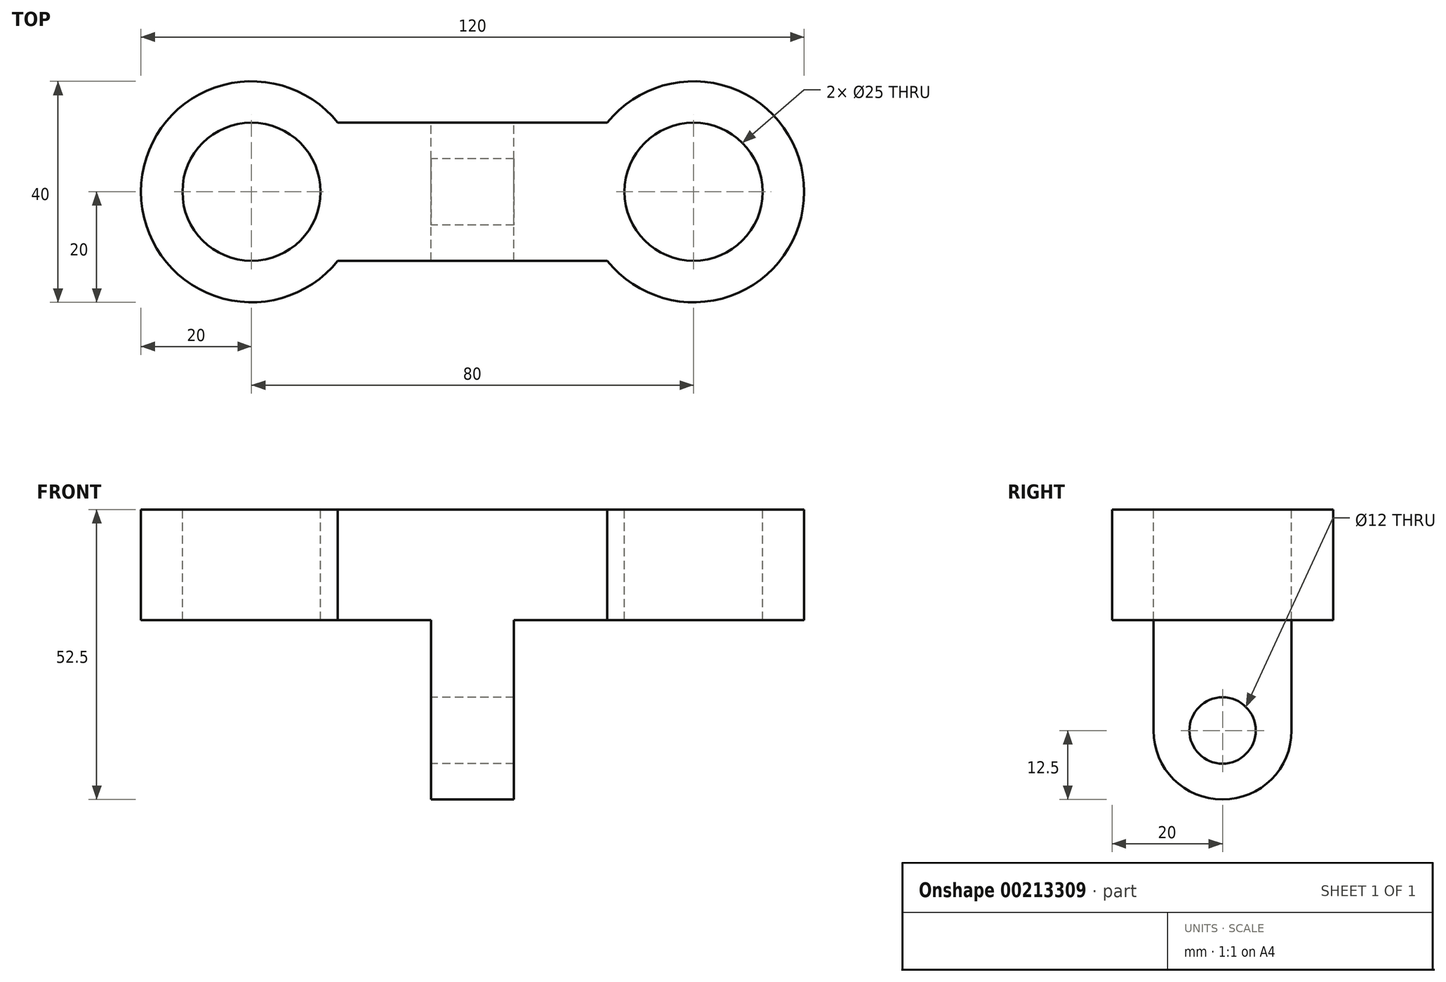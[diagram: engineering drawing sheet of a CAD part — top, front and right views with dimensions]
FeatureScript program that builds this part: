
annotation { "Feature Type Name" : "Feature", "Feature Type Description" : "" }
export const myFeature = defineFeature(function(context is Context, id is Id, definition is map)
    precondition{}
    {
        {
            var Q0;
            Q0=qCreatedBy(makeId("Top.planeOp"),FACE);
            var sketch = newSketch(context, id + "F0", { "sketchPlane" : qUnion([Q0])});
            skCircle(sketch, "E0", {"center": v(-40, 0) * mm, "radius": 12.5 * mm});
            skCircle(sketch, "E1", {"center": v(40, 0) * mm, "radius": 12.5 * mm});
            skArc(sketch, "E2", {"start": v(-24.39, 12.5) * mm, "mid": v(-60, 0) * mm, "end": v(-24.39, -12.5) * mm});
            skArc(sketch, "E3", {"start": v(24.39, -12.5) * mm, "mid": v(60, 0) * mm, "end": v(24.39, 12.5) * mm});
            skLineSegment(sketch, "E4", {"start": v(-24.39, -12.5) * mm, "end": v(24.39, -12.5) * mm});
            skLineSegment(sketch, "E5.trimOffspring", {"start": v(-24.39, 12.5) * mm, "end": v(24.39, 12.5) * mm});
            skSolve(sketch);
        }
        {
            var Q0;
            Q0=makeQuery(id+"F0.imprint","IMPRINT",FACE,{"disambiguationData":[TD([[makeQuery(id+"F0.imprint","IMPRINT",EDGE,{"derivedFrom":sQuery(id+"F0.wireOp",EDGE,"E0")}),-1.0]])]});
            extrude(context, id + "F1", {"entities" : qUnion([Q0]), "endBound" : BoundingType.SYMMETRIC, "oppositeDirection" : true, "depth" : 20 * mm});
        }
        {
            var Q0;
            Q0=qCreatedBy(makeId("Right.planeOp"),FACE);
            var sketch = newSketch(context, id + "F2", { "sketchPlane" : qUnion([Q0])});
            skPoint(sketch, "E6.0", {"position": v(-12.5, -10) * mm});
            skPoint(sketch, "E7.0", {"position": v(12.5, -10) * mm});
            skLineSegment(sketch, "E8", {"start": v(-12.5, -10) * mm, "end": v(12.5, -10) * mm});
            skLineSegment(sketch, "E9", {"start": v(-12.5, -10) * mm, "end": v(-12.5, -30) * mm});
            skLineSegment(sketch, "E10", {"start": v(12.5, -10) * mm, "end": v(12.5, -30) * mm});
            skArc(sketch, "E11", {"start": v(-12.5, -30) * mm, "mid": v(0, -42.5) * mm, "end": v(12.5, -30) * mm});
            skCircle(sketch, "E12", {"center": v(0, -30) * mm, "radius": 6 * mm});
            skSolve(sketch);
        }
        {
            var Q0;
            Q0=makeQuery(id+"F2.imprint","IMPRINT",FACE,{"disambiguationData":[TD([[makeQuery(id+"F2.imprint","IMPRINT",EDGE,{"derivedFrom":sQuery(id+"F2.wireOp",EDGE,"E8")}),-1.0]])]});
            extrude(context, id + "F3", {"entities" : qUnion([Q0]), "operationType" : NewBodyOperationType.ADD, "endBound" : BoundingType.SYMMETRIC, "depth" : 15 * mm});
        }
    });
